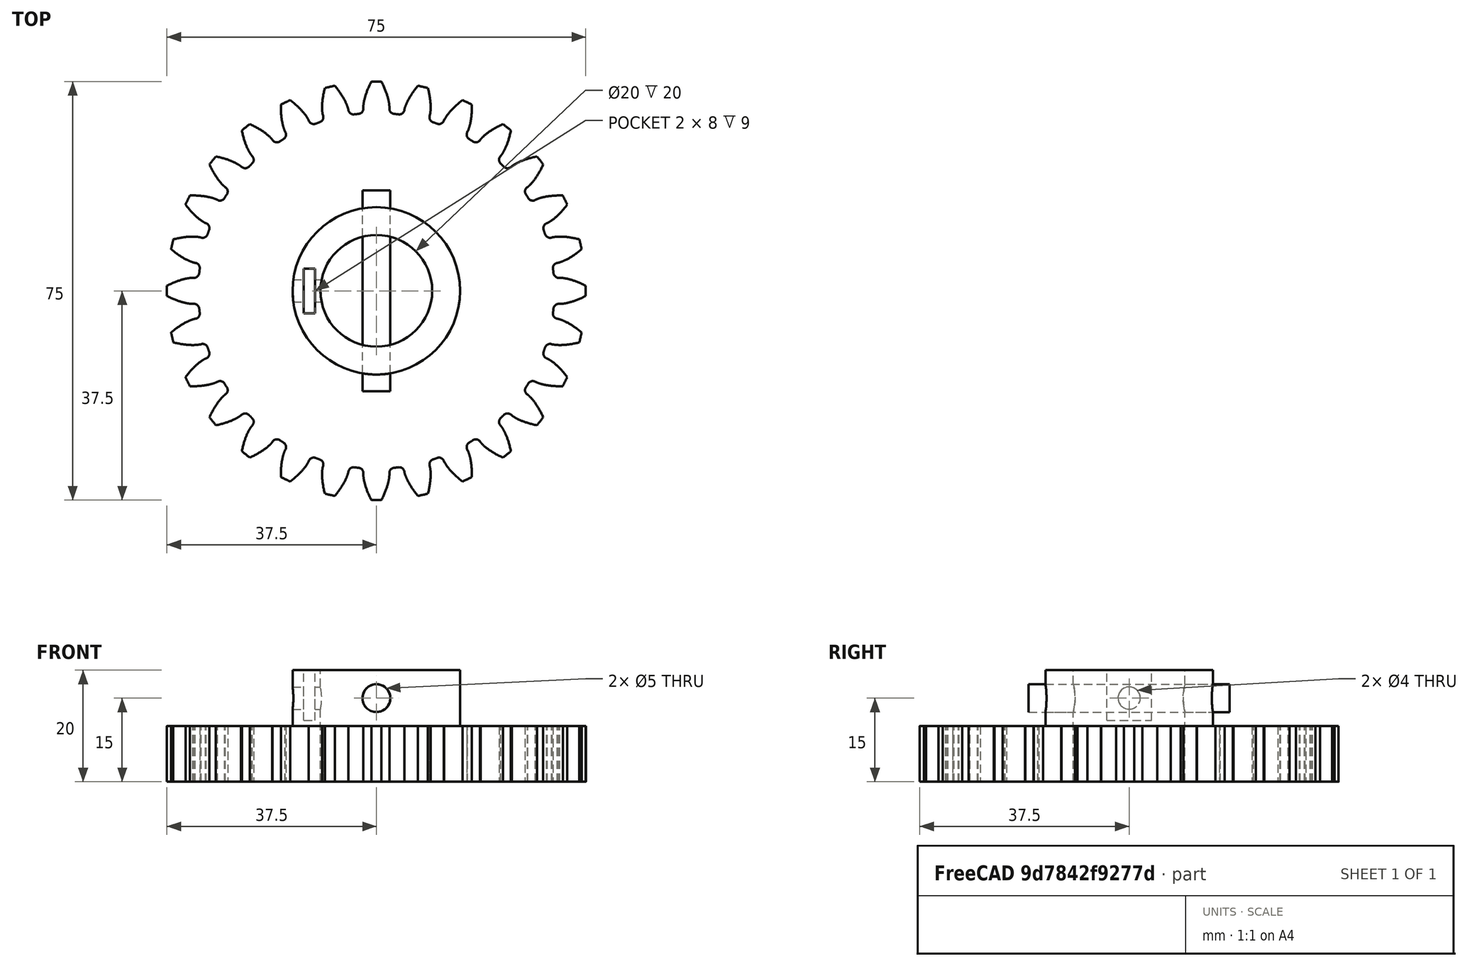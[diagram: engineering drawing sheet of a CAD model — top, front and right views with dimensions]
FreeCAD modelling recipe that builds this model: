
FCSTD DOCUMENT  (FreeCAD 0.18R4 (GitTag))
Label: Engranaje1
License: All rights reserved
LicenseURL: http://en.wikipedia.org/wiki/All_rights_reserved
objects: Part::Cylinder×8, Part::Cut×8, Part::Part2DObjectPython×1, Part::Extrusion×1, Part::MultiFuse×1, Part::Box×1
note: 20 computed .brp shape members not serialized (recipe doc carries the construction recipe); baked Part::Feature solids carry a one-line shape summary decoded from their .brp

FEATURE [Part::Cylinder] Cylinder003  label="Cilindro003"
  Angle = 360
  AttacherType = Attacher::AttachEngine3D
  Height = 10
  Radius = 3
FEATURE [Part::Part2DObjectPython] InvoluteGear  # Draft 2D object (typed FeaturePython)
  ExternalGear = true
  HighPrecision = true
  Modules = 2.5
  NumberOfTeeth = 28
  PressureAngle = 20
FEATURE [Part::Extrusion] Extrude
  Base = -> InvoluteGear
  Dir = (0,0,1)
  DirMode = 2
  FaceMakerClass = Part::FaceMakerBullseye
  LengthFwd = 10
  LengthRev = 0
  Solid = true
  Symmetric = false
FEATURE [Part::Cut] Cut002
  Base = -> Extrude
  Tool = -> Cylinder003
FEATURE [Part::Cylinder] Cylinder  label="Cilindro"
  Angle = 360
  AttacherType = Attacher::AttachEngine3D
  Height = 10
  Radius = 2
FEATURE [Part::Cut] Cut
  Base = -> Cut002
  Tool = -> Cylinder
FEATURE [Part::Cylinder] Cylinder004  label="Cilindro004"
  Angle = 360
  AttacherType = Attacher::AttachEngine3D
  Height = 10
  Radius = 10
FEATURE [Part::Cylinder] Cylinder005  label="Cilindro005"
  Angle = 360
  AttacherType = Attacher::AttachEngine3D
  Height = 10
  Placement = pos=(0,0,10) rot=(0,0,1;0rad)
  Radius = 15
FEATURE [Part::Cut] Cut003
  Base = -> Cylinder005
  Tool = -> Cylinder004
FEATURE [Part::Cut] Cut004
  Base = -> Cut003
  Tool = -> Cylinder
FEATURE [Part::Cylinder] Cylinder006  label="Cilindro006"
  Angle = 360
  AttacherType = Attacher::AttachEngine3D
  Height = 40
  Placement = pos=(0,0,-15) rot=(0,0,1;0rad)
  Radius = 10
FEATURE [Part::MultiFuse] Fusion
  Shapes = -> [Cut,Cut004]
FEATURE [Part::Cut] Cut005
  Base = -> Fusion
  Tool = -> Cylinder006
FEATURE [Part::Cylinder] Cylinder007  label="Cilindro007"
  Angle = 360
  AttacherType = Attacher::AttachEngine3D
  Height = 10
  Placement = pos=(-17,0,15) rot=(0,1,0;1.5708rad)
  Radius = 2
FEATURE [Part::Cut] Cut006
  Base = -> Cut005
  Tool = -> Cylinder007
FEATURE [Part::Box] Box  label="Cubo"
  AttacherType = Attacher::AttachEngine3D
  Height = 10
  Length = 2
  Placement = pos=(-13,-4,11) rot=(0,0,1;0rad)
  Width = 8
FEATURE [Part::Cut] Cut007
  Base = -> Cut006
  Tool = -> Box
FEATURE [Part::Cylinder] Cylinder008  label="Cilindro008"
  Angle = 360
  AttacherType = Attacher::AttachEngine3D
  Height = 30
  Placement = pos=(0,-15,15) rot=(-0.306715,0.673025,0.673025;2.54638rad)
  Radius = 2.5
FEATURE [Part::Cylinder] Cylinder009  label="Pasador 5mm"
  Angle = 360
  AttacherType = Attacher::AttachEngine3D
  Height = 36
  Placement = pos=(0,-18,15) rot=(-0.306715,0.673025,0.673025;2.54643rad)
  Radius = 2.5
FEATURE [Part::Cut] Cut008  label="EngranajeEjeZ"
  Base = -> Cut007
  Tool = -> Cylinder008
